# Revit family: 265-91-001 DN350-400
name_source: partatom
category: Pipe Accessories
units: mm (PartAtom-declared; Revit-internal decimal feet)

## family parameters
Always vertical = Yes
Cut with Voids When Loaded = No
Part Type = Valve - Breaks Into
Round Connector Dimension = Use Diameter
Shared = No
Work Plane-Based = No

## types (4) — shared parameters
25 = 25 mm  [stored 0.082021 ft]
Bolt.no = 16 mm  [stored 0.0524934 ft]
DN350_PN10 = 265-9-0350-11-04036401
DN350_PN16 = 265-9-0350-10-14036400
DN400_PN10 = 265-9-0400-11-04036401
DN400_PN16 = 265-9-0400-10-14036400
Description_ = AVK DISMANTLING JOINT WITH CENTRE FLANGE, PN10/16
Raised_dis = 4 mm  [stored 0.0131234 ft]
Search_table = 265-91-001 DN350-400
URL_product_pages = https://www.avkvalves.com
zero-valued in all types: Default Elevation

## per-type parameters (varying)
| type | B1 | Bore | D | DN | FL_T | FL_T/2 | L | L1 | L11 | L2 | L3 | Nut_T | PCD | PN | S | S11 | T | T1 | offset | raised_R |
| DN350_PN16 | 34 mm | 175 mm  [stored 0.574147 ft] | 260 mm  [stored 0.853018 ft] | 350 mm  [stored 1.14829 ft] | 27 mm  [stored 0.0885827 ft] | 13 mm  [stored 0.0426509 ft] | 420 mm | 177 mm | 260 mm  [stored 0.853018 ft] | 27 mm  [stored 0.0885827 ft] | 13 mm  [stored 0.0426509 ft] | 20 mm  [stored 0.0656168 ft] | 235 mm  [stored 0.770997 ft] | 16 mm  [stored 0.0524934 ft] | 24 mm  [stored 0.0787402 ft] | 32 mm  [stored 0.104987 ft] | 8 mm  [stored 0.0262467 ft] | 20 mm  [stored 0.0656168 ft] | 8 mm  [stored 0.0262467 ft] | 195 mm  [stored 0.639764 ft] |
| DN350_PN10 | 30 mm  [stored 0.0984252 ft] | 175 mm  [stored 0.574147 ft] | 253 mm | 350 mm  [stored 1.14829 ft] | 25 mm  [stored 0.082021 ft] | 12 mm  [stored 0.0393701 ft] | 370 mm | 156 mm | 230 mm  [stored 0.754593 ft] | 24 mm  [stored 0.0787402 ft] | 12 mm  [stored 0.0393701 ft] | 18 mm | 230 mm  [stored 0.754593 ft] | 10 mm  [stored 0.0328084 ft] | 20 mm  [stored 0.0656168 ft] | 27 mm  [stored 0.0885827 ft] | 7 mm  [stored 0.0229659 ft] | 18 mm | 7 mm  [stored 0.0229659 ft] | 189 mm |
| DN400_PN16 | 34 mm | 200 mm  [stored 0.656168 ft] | 290 mm  [stored 0.951444 ft] | 400 mm | 28 mm  [stored 0.0918635 ft] | 14 mm  [stored 0.0459318 ft] | 430 mm | 184 mm | 270 mm  [stored 0.885827 ft] | 28 mm  [stored 0.0918635 ft] | 14 mm  [stored 0.0459318 ft] | 21 mm  [stored 0.0688976 ft] | 263 mm | 16 mm  [stored 0.0524934 ft] | 27 mm  [stored 0.0885827 ft] | 36 mm  [stored 0.11811 ft] | 8 mm  [stored 0.0262467 ft] | 21 mm  [stored 0.0688976 ft] | 9 mm  [stored 0.0295276 ft] | 218 mm |
| DN400_PN10 | 30 mm  [stored 0.0984252 ft] | 200 mm  [stored 0.656168 ft] | 283 mm | 400 mm | 25 mm  [stored 0.082021 ft] | 12 mm  [stored 0.0393701 ft] | 380 mm | 156 mm | 230 mm  [stored 0.754593 ft] | 25 mm  [stored 0.082021 ft] | 12 mm  [stored 0.0393701 ft] | 18 mm | 258 mm | 10 mm  [stored 0.0328084 ft] | 24 mm  [stored 0.0787402 ft] | 32 mm  [stored 0.104987 ft] | 7 mm  [stored 0.0229659 ft] | 18 mm | 8 mm  [stored 0.0262467 ft] | 212 mm |

note: [stored X ft] marks values corroborated as IEEE doubles in the binary element streams (Revit-internal decimal feet)

## geometry (parser evidence)
native form markers: Sweep x11
no freeform markers — native parametric forms only
